# Revit family: RG200
name_source: partatom
category: Specialty Equipment
revit_build: Autodesk Revit MEP 2012 (Build: 20110916_2132(x64)
units: mm (PartAtom-declared; Revit-internal decimal feet)

## types (1)
- RG200
    Apparent Power = 0 VA
    Assembly Code = E1090320
    Conn Conduit = Yes
    Cycle = 50 Hz
    Depth = 485 mm  [stored 1.59121 ft]
    Description = VEGETABLE PREPARATION MACHINE 7 KG/MINUTE
    Elec Conn Connection Height = 342 mm  [stored 1.12205 ft]
    FL Amps = 0 A
    Height = 530 mm  [stored 1.73885 ft]
    Manufacturer = HALLDE
    Max Overcurrent Protection = 10 A
    Min Ckt Ampacity = 0 A
    Model = RG-200
    Phase = 1
    URL = www.hallde.com
    Volts = 230 V
    Watts = 370 W
    Weight = 18 kg
    Width = 245 mm  [stored 0.803806 ft]

note: [stored X ft] marks values corroborated as IEEE doubles in the binary element streams (Revit-internal decimal feet)

## geometry (parser evidence)
native form markers: Blend x12, Sweep x1
no freeform markers — native parametric forms only
